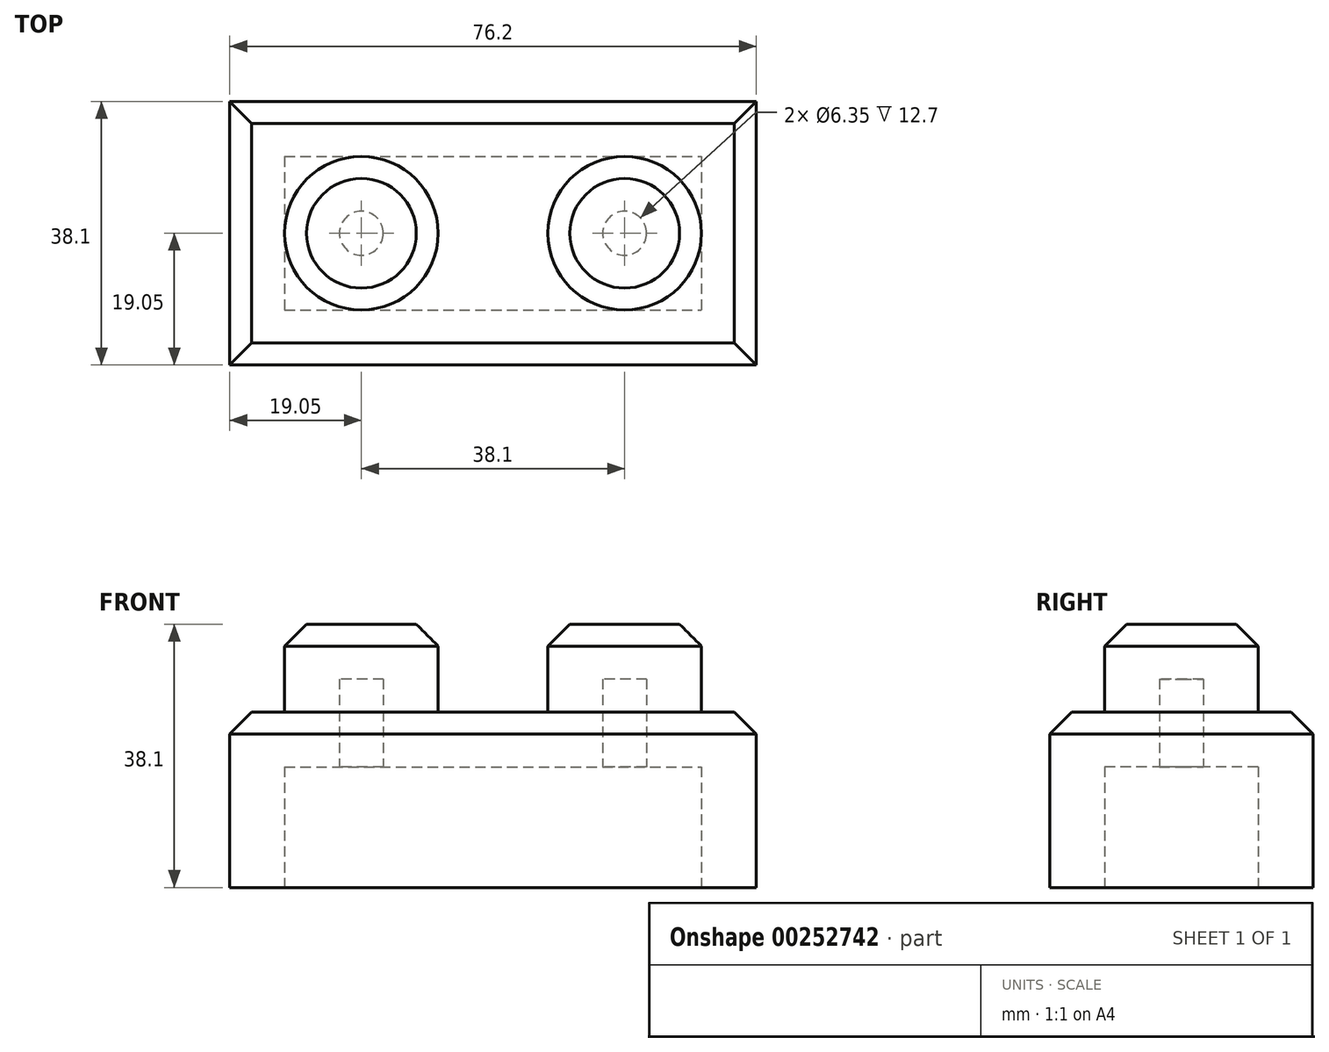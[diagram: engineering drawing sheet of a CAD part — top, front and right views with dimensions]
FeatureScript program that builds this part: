
annotation { "Feature Type Name" : "Feature", "Feature Type Description" : "" }
export const myFeature = defineFeature(function(context is Context, id is Id, definition is map)
    precondition{}
    {
        {
            var Q0;
            Q0=qCreatedBy(makeId("Top.planeOp"),FACE);
            var sketch = newSketch(context, id + "F0", { "sketchPlane" : qUnion([Q0])});
            skLineSegment(sketch, "E0.bottom", {"start": v(0, 38.1) * mm, "end": v(76.2, 38.1) * mm});
            skLineSegment(sketch, "E0.top", {"start": v(0, 0) * mm, "end": v(76.2, 0) * mm});
            skLineSegment(sketch, "E0.left", {"start": v(0, 38.1) * mm, "end": v(0, 0) * mm});
            skLineSegment(sketch, "E0.right", {"start": v(76.2, 38.1) * mm, "end": v(76.2, 0) * mm});
            skSolve(sketch);
        }
        {
            var Q0;
            Q0 = qSketchRegion(id + "F0", true);
            extrude(context, id + "F1", {"entities" : qUnion([Q0]), "depth" : 25.4 * mm});
        }
        {
            var Q0;
            Q0=makeQuery(id+"F1.opExtrude","CAP_FACE",FACE,{"disambiguationData":[OSD([sQuery(id+"F0.wireOp",EDGE,"E0.bottom"),sQuery(id+"F0.wireOp",EDGE,"E0.top"),sQuery(id+"F0.wireOp",EDGE,"E0.left"),sQuery(id+"F0.wireOp",EDGE,"E0.right")])],"isStart":false});
            var sketch = newSketch(context, id + "F2", { "sketchPlane" : qUnion([Q0])});
            skCircle(sketch, "E1", {"center": v(19.05, 19.05) * mm, "radius": 11.11 * mm});
            skCircle(sketch, "E2", {"center": v(57.15, 19.05) * mm, "radius": 11.11 * mm});
            skSolve(sketch);
        }
        {
            var Q0;
            Q0 = qSketchRegion(id + "F2", true);
            extrude(context, id + "F3", {"entities" : qUnion([Q0]), "operationType" : NewBodyOperationType.ADD, "depth" : 12.7 * mm});
        }
        {
            var Q0;
            Q0=makeQuery(id+"F1.opExtrude","CAP_FACE",FACE,{"disambiguationData":[OSD([sQuery(id+"F0.wireOp",EDGE,"E0.bottom"),sQuery(id+"F0.wireOp",EDGE,"E0.top"),sQuery(id+"F0.wireOp",EDGE,"E0.left"),sQuery(id+"F0.wireOp",EDGE,"E0.right")])],"isStart":true});
            shell(context, id + "F4", {"entities" : qUnion([Q0]), "thickness" : 7.94 * mm});
        }
        {
            var Q0;
            Q0=makeQuery(id+"F3.opExtrude","CAP_EDGE",EDGE,{"disambiguationData":[OSD([sQuery(id+"F2.wireOp",EDGE,"E1")])],"isStart":false});
            var Q1;
            Q1=makeQuery(id+"F3.opExtrude","CAP_EDGE",EDGE,{"disambiguationData":[OSD([sQuery(id+"F2.wireOp",EDGE,"E2")])],"isStart":false});
            var Q2;
            Q2=makeQuery(id+"F1.opExtrude","CAP_EDGE",EDGE,{"disambiguationData":[OSD([sQuery(id+"F0.wireOp",EDGE,"E0.top")])],"isStart":false});
            var Q3;
            Q3=makeQuery(id+"F1.opExtrude","CAP_EDGE",EDGE,{"disambiguationData":[OSD([sQuery(id+"F0.wireOp",EDGE,"E0.bottom")])],"isStart":false});
            var Q4;
            Q4=makeQuery(id+"F1.opExtrude","CAP_EDGE",EDGE,{"disambiguationData":[OSD([sQuery(id+"F0.wireOp",EDGE,"E0.left")])],"isStart":false});
            var Q5;
            Q5=makeQuery(id+"F1.opExtrude","CAP_EDGE",EDGE,{"disambiguationData":[OSD([sQuery(id+"F0.wireOp",EDGE,"E0.right")])],"isStart":false});
            chamfer(context, id + "F5", {"entities" : qUnion([Q0, Q1, Q2, Q3, Q4, Q5]), "chamferType" : ChamferType.OFFSET_ANGLE, "width" : 3.17 * mm, "oppositeDirection" : false, "angle" : 45 * degree, "tangentPropagation" : true});
        }
    });
